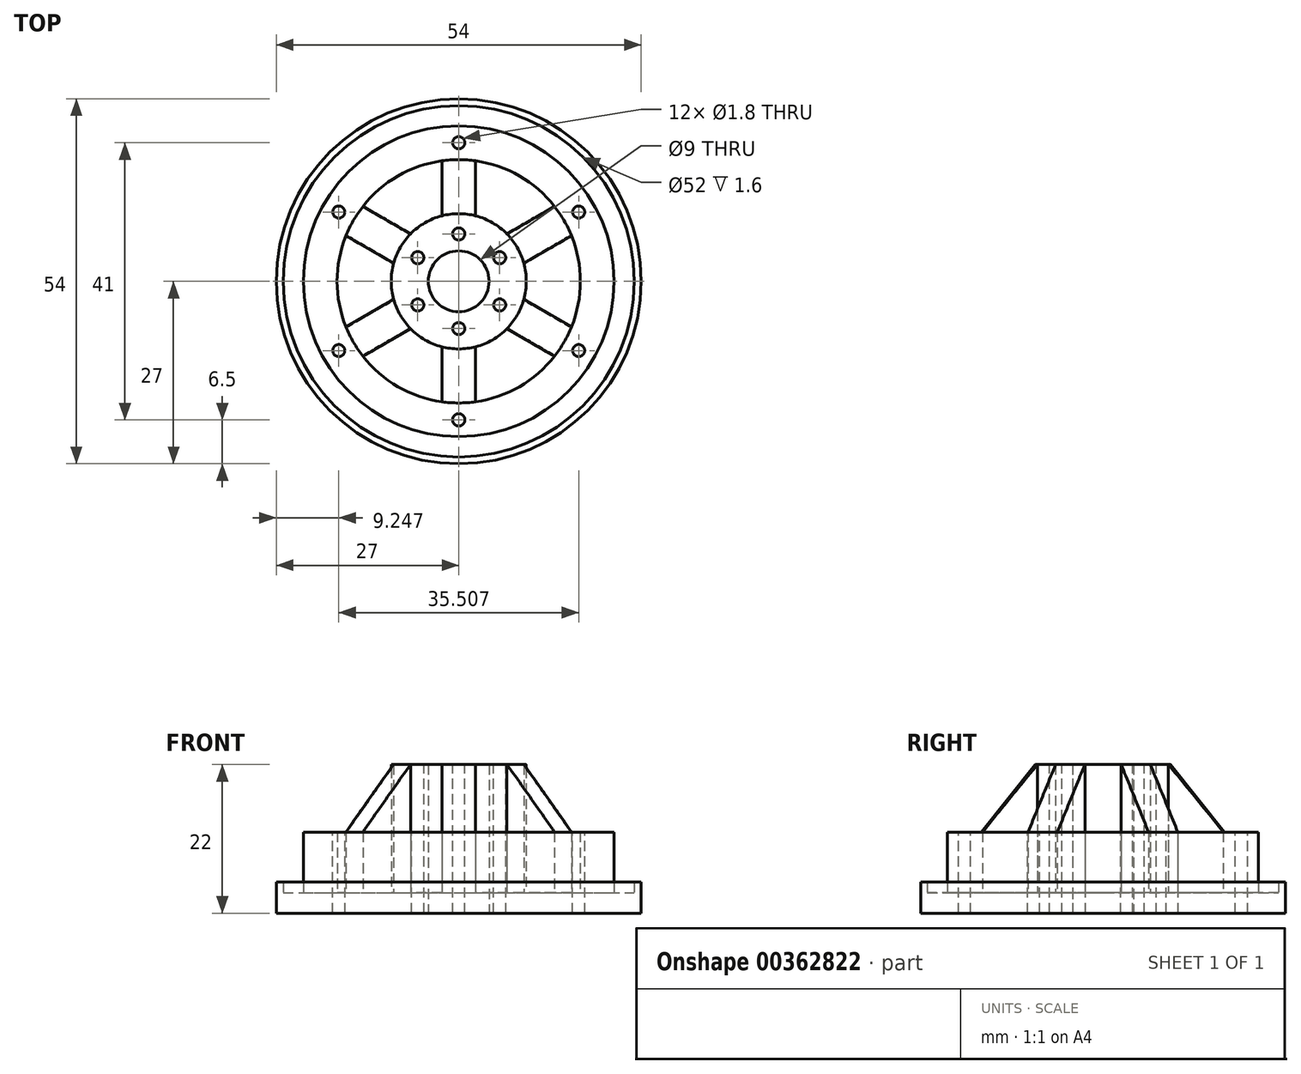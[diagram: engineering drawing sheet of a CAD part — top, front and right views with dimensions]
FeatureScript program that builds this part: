
annotation { "Feature Type Name" : "Feature", "Feature Type Description" : "" }
export const myFeature = defineFeature(function(context is Context, id is Id, definition is map)
    precondition{}
    {
        {
            var Q0;
            Q0=qCreatedBy(makeId("Front.planeOp"),FACE);
            var sketch = newSketch(context, id + "F0", { "sketchPlane" : qUnion([Q0])});
            skLineSegment(sketch, "E0", {"start": v(27, 0) * mm, "end": v(27, 4.6) * mm});
            skLineSegment(sketch, "E1", {"start": v(27, 4.6) * mm, "end": v(26, 4.6) * mm});
            skLineSegment(sketch, "E2", {"start": v(26, 4.6) * mm, "end": v(26, 3) * mm});
            skLineSegment(sketch, "E3", {"start": v(26, 3) * mm, "end": v(23, 3) * mm});
            skLineSegment(sketch, "E4", {"start": v(23, 3) * mm, "end": v(23, 12) * mm});
            skLineSegment(sketch, "E5", {"start": v(23, 12) * mm, "end": v(10, 12) * mm});
            skLineSegment(sketch, "E6", {"start": v(10, 12) * mm, "end": v(10, 22) * mm});
            skLineSegment(sketch, "E7", {"start": v(10, 22) * mm, "end": v(4.5, 22) * mm});
            skLineSegment(sketch, "E8", {"start": v(4.5, 22) * mm, "end": v(4.5, 0) * mm});
            skLineSegment(sketch, "E9", {"start": v(4.5, 0) * mm, "end": v(27, 0) * mm});
            skLineSegment(sketch, "E10", {"start": v(0, 0) * mm, "end": v(0, 22.65) * mm, "construction": true});
            skLineSegment(sketch, "E11", {"start": v(10, 22) * mm, "end": v(18, 12) * mm});
            skSolve(sketch);
        }
        {
            var Q0;
            Q0=makeQuery(id+"F0.imprint","IMPRINT",FACE,{"disambiguationData":[TD([[makeQuery(id+"F0.imprint","IMPRINT",EDGE,{"derivedFrom":sQuery(id+"F0.wireOp",EDGE,"E0")}),1.0]])]});
            var Q1;
            {var subQ0=sQuery(id+"F0.wireOp",EDGE,"E6");Q1=makeQuery(id+"F0.imprint","IMPRINT",FACE,{"disambiguationData":[TD([[makeQuery(id+"F0.imprint","IMPRINT",EDGE,{"derivedFrom":subQ0}),-1.0]])]});}
            var Q2;
            Q2=sQuery(id+"F0.wireOp",EDGE,"E10");
            revolve(context, id + "F1", {"entities" : qUnion([Q0, Q1]), "axis" : qUnion([Q2]), "revolveType" : RevolveType.FULL});
        }
        {
            var Q0;
            Q0=makeQuery(id+"F1.opRevolve","SWEPT_FACE",FACE,{"disambiguationData":[OSD([sQuery(id+"F0.wireOp",EDGE,"E5")])]});
            var sketch = newSketch(context, id + "F2", { "sketchPlane" : qUnion([Q0])});
            skCircle(sketch, "E12.0", {"center": v(0, 0) * mm, "radius": 10 * mm});
            skLineSegment(sketch, "E13", {"start": v(0, 0) * mm, "end": v(0, 18) * mm, "construction": true});
            skCircle(sketch, "E14.0", {"center": v(0, 0) * mm, "radius": 18 * mm});
            skLineSegment(sketch, "E15", {"start": v(-2.5, 17.83) * mm, "end": v(-2.5, 9.68) * mm});
            skLineSegment(sketch, "E16.MirrorCS", {"start": v(2.5, 17.83) * mm, "end": v(2.5, 9.68) * mm});
            skLineSegment(sketch, "E17.1.0", {"start": v(-16.69, 6.75) * mm, "end": v(-9.64, 2.68) * mm});
            skLineSegment(sketch, "E17.1.1", {"start": v(-14.19, 11.08) * mm, "end": v(-7.14, 7) * mm});
            skLineSegment(sketch, "E17.2.0", {"start": v(-14.19, -11.08) * mm, "end": v(-7.14, -7) * mm});
            skLineSegment(sketch, "E17.2.1", {"start": v(-16.69, -6.75) * mm, "end": v(-9.64, -2.68) * mm});
            skLineSegment(sketch, "E17.3.0", {"start": v(2.5, -17.83) * mm, "end": v(2.5, -9.68) * mm});
            skLineSegment(sketch, "E17.3.1", {"start": v(-2.5, -17.83) * mm, "end": v(-2.5, -9.68) * mm});
            skLineSegment(sketch, "E17.4.0", {"start": v(16.69, -6.75) * mm, "end": v(9.64, -2.68) * mm});
            skLineSegment(sketch, "E17.4.1", {"start": v(14.19, -11.08) * mm, "end": v(7.14, -7) * mm});
            skLineSegment(sketch, "E17.5.0", {"start": v(14.19, 11.08) * mm, "end": v(7.14, 7) * mm});
            skLineSegment(sketch, "E17.5.1", {"start": v(16.69, 6.75) * mm, "end": v(9.64, 2.68) * mm});
            skSolve(sketch);
        }
        {
            var Q0;
            {var subQ0=sQuery(id+"F2.wireOp",EDGE,"E15");Q0=makeQuery(id+"F2.imprint","IMPRINT",FACE,{"disambiguationData":[TD([[makeQuery(id+"F2.imprint","IMPRINT",EDGE,{"derivedFrom":subQ0}),-1.0]])]});}
            var Q1;
            {var subQ0=sQuery(id+"F2.wireOp",EDGE,"E17.1.0");Q1=makeQuery(id+"F2.imprint","IMPRINT",FACE,{"disambiguationData":[TD([[makeQuery(id+"F2.imprint","IMPRINT",EDGE,{"derivedFrom":subQ0}),-1.0]])]});}
            var Q2;
            {var subQ0=sQuery(id+"F2.wireOp",EDGE,"E17.2.0");Q2=makeQuery(id+"F2.imprint","IMPRINT",FACE,{"disambiguationData":[TD([[makeQuery(id+"F2.imprint","IMPRINT",EDGE,{"derivedFrom":subQ0}),-1.0]])]});}
            var Q3;
            {var subQ0=sQuery(id+"F2.wireOp",EDGE,"E17.3.0");Q3=makeQuery(id+"F2.imprint","IMPRINT",FACE,{"disambiguationData":[TD([[makeQuery(id+"F2.imprint","IMPRINT",EDGE,{"derivedFrom":subQ0}),-1.0]])]});}
            var Q4;
            {var subQ0=sQuery(id+"F2.wireOp",EDGE,"E17.4.0");Q4=makeQuery(id+"F2.imprint","IMPRINT",FACE,{"disambiguationData":[TD([[makeQuery(id+"F2.imprint","IMPRINT",EDGE,{"derivedFrom":subQ0}),-1.0]])]});}
            var Q5;
            {var subQ0=sQuery(id+"F2.wireOp",EDGE,"E16.MirrorCS");Q5=makeQuery(id+"F2.imprint","IMPRINT",FACE,{"disambiguationData":[TD([[makeQuery(id+"F2.imprint","IMPRINT",EDGE,{"derivedFrom":subQ0}),1.0]])]});}
            extrude(context, id + "F3", {"entities" : qUnion([Q0, Q1, Q2, Q3, Q4, Q5]), "operationType" : NewBodyOperationType.REMOVE, "depth" : 25 * mm, "hasSecondDirection" : true, "secondDirectionOppositeDirection" : true, "secondDirectionDepth" : 9 * mm});
        }
        {
            var Q0;
            Q0=makeQuery(id+"F1.opRevolve","SWEPT_FACE",FACE,{"disambiguationData":[OSD([sQuery(id+"F0.wireOp",EDGE,"E7")])]});
            var sketch = newSketch(context, id + "F4", { "sketchPlane" : qUnion([Q0])});
            skLineSegment(sketch, "E18", {"start": v(0, 0) * mm, "end": v(0, 7) * mm, "construction": true});
            skCircle(sketch, "E19", {"center": v(0, 7) * mm, "radius": 0.9 * mm});
            skLineSegment(sketch, "E20", {"start": v(0, 7) * mm, "end": v(0, 20.5) * mm, "construction": true});
            skPoint(sketch, "E20.endSnap0", {"position": v(0, 10) * mm});
            skCircle(sketch, "E21", {"center": v(0, 20.5) * mm, "radius": 0.9 * mm});
            skCircle(sketch, "E22.1.0", {"center": v(-6.06, 3.5) * mm, "radius": 0.9 * mm});
            skCircle(sketch, "E22.1.1", {"center": v(-17.75, 10.25) * mm, "radius": 0.9 * mm});
            skCircle(sketch, "E22.2.0", {"center": v(-6.06, -3.5) * mm, "radius": 0.9 * mm});
            skCircle(sketch, "E22.2.1", {"center": v(-17.75, -10.25) * mm, "radius": 0.9 * mm});
            skCircle(sketch, "E22.3.0", {"center": v(0, -7) * mm, "radius": 0.9 * mm});
            skCircle(sketch, "E22.3.1", {"center": v(0, -20.5) * mm, "radius": 0.9 * mm});
            skCircle(sketch, "E22.4.0", {"center": v(6.06, -3.5) * mm, "radius": 0.9 * mm});
            skCircle(sketch, "E22.4.1", {"center": v(17.75, -10.25) * mm, "radius": 0.9 * mm});
            skCircle(sketch, "E22.5.0", {"center": v(6.06, 3.5) * mm, "radius": 0.9 * mm});
            skCircle(sketch, "E22.5.1", {"center": v(17.75, 10.25) * mm, "radius": 0.9 * mm});
            skPoint(sketch, "E22.center", {"position": v(0, 0) * mm});
            skSolve(sketch);
        }
        {
            var Q0;
            Q0 = qSketchRegion(id + "F4", true);
            extrude(context, id + "F5", {"entities" : qUnion([Q0]), "operationType" : NewBodyOperationType.REMOVE, "endBound" : BoundingType.THROUGH_ALL, "oppositeDirection" : true, "depth" : 25 * mm});
        }
    });
